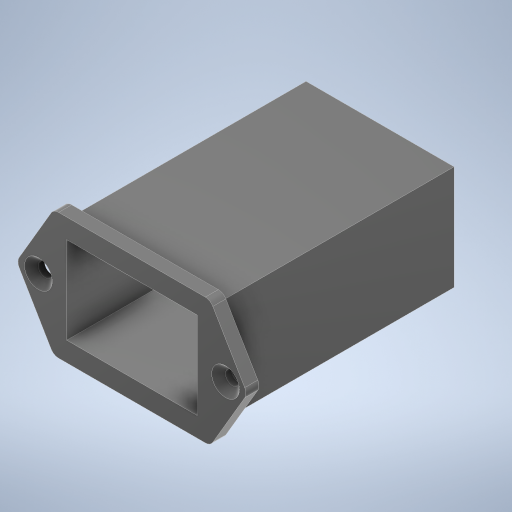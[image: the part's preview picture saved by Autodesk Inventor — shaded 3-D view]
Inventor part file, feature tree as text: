
AUTODESK INVENTOR PART (.ipt)
format: ipt  version: 2023 (Build 270158000, 158)  size: 259,072 bytes
history: native  units: in
note: dims shown in document units (in); Inventor stores cm internally (conversion verified against a paired STEP export)
features: sketch x4, extrude x3, hole x1
ambient origin geometry x8: Origin, YZ Plane, XZ Plane, XY Plane, X Axis, Y Axis, Z Axis, Center Point
bodies: Solid1 (feature_tree)
feature tree (8):
  extrude  "Extrusion1"  Depth=1.0433in
  hole  "Hole1"  [1 undecoded]
  extrude  "Extrusion2"  Depth=0.0787in
  extrude  "Extrusion3"  Depth=0.1181in TaperAngle=0.0deg
  sketch  "Sketch1"  dims[d0=2.0866in d1=1.0433in]
  sketch  "Sketch2"  dims[d2=0.5709in d3=1.4173in]
  sketch  "Sketch3"  dims[d4=0.7087in d5=0.0787in]
  sketch  "Sketch4"  dims[d6=0.0787in d7=0.1181in d8=0.0in d9=1.6929in d10=0.8465in d11=0.126in d12=0.3389in d13=0.25in d14=0.0787in d15=90.0deg d16=0.315in d17=0.8108in d18=0.9449in d19=1.3386in d20=0.6693in d21=0.4724in d22=2.126in d23=0.0in d24=1.1811in d25=0.7874in d26=0.5906in d27=0.3937in d28=1.9291in d29=0.0in]
note: 1 required parameter value undecoded (feature->parameter linkage not recoverable at this tier; creation-order binding heuristic only, values carry confidence <= 0.55)
